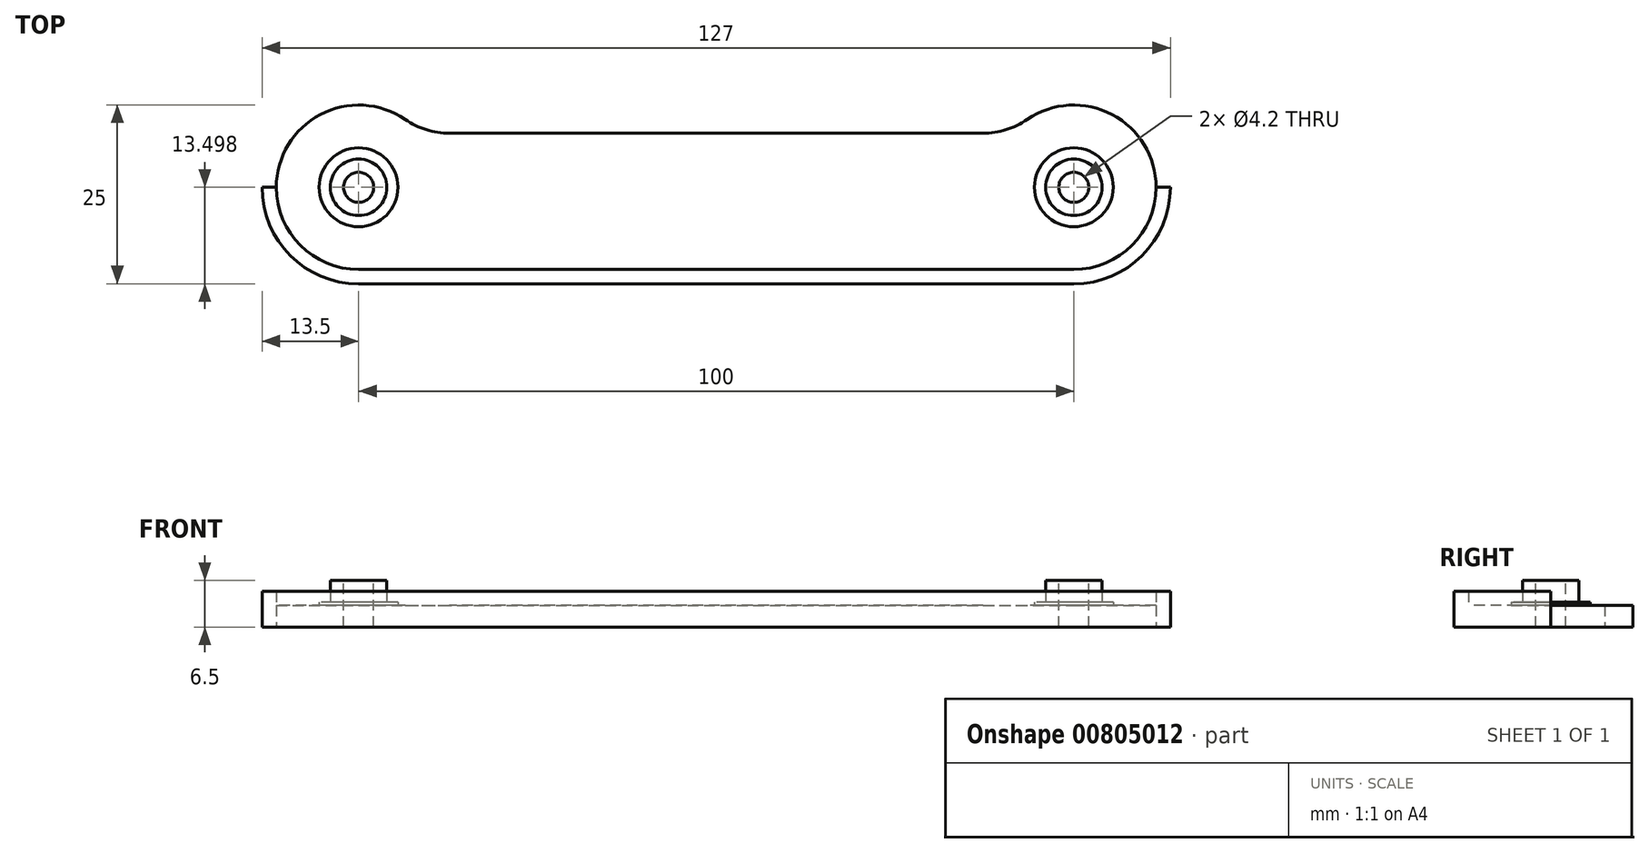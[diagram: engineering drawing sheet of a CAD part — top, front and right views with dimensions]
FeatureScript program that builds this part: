
annotation { "Feature Type Name" : "Feature", "Feature Type Description" : "" }
export const myFeature = defineFeature(function(context is Context, id is Id, definition is map)
    precondition{}
    {
        {
            var Q0;
            Q0=qCreatedBy(makeId("Top.planeOp"),FACE);
            var sketch = newSketch(context, id + "F0", { "sketchPlane" : qUnion([Q0])});
            skLineSegment(sketch, "E0", {"start": v(-50, -12.51) * mm, "end": v(0, -12.51) * mm});
            skArc(sketch, "E1", {"start": v(-50, -12.51) * mm, "mid": v(-61.5, -1.01) * mm, "end": v(-50, 10.49) * mm});
            skArc(sketch, "E2", {"start": v(-50, 10.49) * mm, "mid": v(-46.6, 9.97) * mm, "end": v(-43.5, 8.47) * mm});
            skArc(sketch, "E3", {"start": v(-43.5, 8.47) * mm, "mid": v(-40.54, 7.04) * mm, "end": v(-37.3, 6.55) * mm});
            skLineSegment(sketch, "E4", {"start": v(-37.3, 6.55) * mm, "end": v(0, 6.55) * mm});
            skLineSegment(sketch, "E5.MirrorCS", {"start": v(37.3, 6.55) * mm, "end": v(0, 6.55) * mm});
            skLineSegment(sketch, "E6.MirrorCS", {"start": v(50, -12.51) * mm, "end": v(0, -12.51) * mm});
            skArc(sketch, "E7.MirrorCS", {"start": v(50, -12.51) * mm, "mid": v(61.5, -1.01) * mm, "end": v(50, 10.49) * mm});
            skArc(sketch, "E8.MirrorCS", {"start": v(50, 10.49) * mm, "mid": v(46.6, 9.97) * mm, "end": v(43.5, 8.47) * mm});
            skArc(sketch, "E9.MirrorCS", {"start": v(43.5, 8.47) * mm, "mid": v(40.54, 7.04) * mm, "end": v(37.3, 6.55) * mm});
            skSolve(sketch);
        }
        {
            var Q0;
            Q0 = qSketchRegion(id + "F0", true);
            extrude(context, id + "F1", {"entities" : qUnion([Q0]), "depth" : 3 * mm, "offsetDistance" : 25 * mm});
        }
        {
            var Q0;
            Q0=makeQuery(id+"F0.imprint","IMPRINT",FACE,{"disambiguationData":[TD([[makeQuery(id+"F0.imprint","IMPRINT",EDGE,{"derivedFrom":sQuery(id+"F0.wireOp",EDGE,"E0")}),1.0]])]});
            var sketch = newSketch(context, id + "F2", { "sketchPlane" : qUnion([Q0])});
            skLineSegment(sketch, "E10.0", {"start": v(-50, -14.51) * mm, "end": v(50, -14.51) * mm});
            skArc(sketch, "E10.3", {"start": v(50, -14.51) * mm, "mid": v(59.55, -10.56) * mm, "end": v(63.5, -1.01) * mm});
            skArc(sketch, "E10.5", {"start": v(-63.5, -1.01) * mm, "mid": v(-59.55, -10.56) * mm, "end": v(-50, -14.51) * mm});
            skArc(sketch, "E11.0.0", {"start": v(50, -12.51) * mm, "mid": v(58.13, -9.14) * mm, "end": v(61.5, -1.01) * mm});
            skArc(sketch, "E11.0.4", {"start": v(-61.5, -1.01) * mm, "mid": v(-58.13, -9.14) * mm, "end": v(-50, -12.51) * mm});
            skLineSegment(sketch, "E11.0.5", {"start": v(-50, -12.51) * mm, "end": v(50, -12.51) * mm});
            skLineSegment(sketch, "E12", {"start": v(-61.5, -1.01) * mm, "end": v(-63.5, -1.01) * mm});
            skLineSegment(sketch, "E13.MirrorCS", {"start": v(61.5, -1.01) * mm, "end": v(63.5, -1.01) * mm});
            skPoint(sketch, "E11.0.3.end.orphan", {"position": v(-43.5, 8.47) * mm});
            skPoint(sketch, "E11.0.2.end.orphan", {"position": v(-37.3, 6.55) * mm});
            skPoint(sketch, "E11.0.1.end.orphan", {"position": v(37.3, 6.55) * mm});
            skPoint(sketch, "E14.orphan", {"position": v(43.5, 8.47) * mm});
            skSolve(sketch);
        }
        {
            var Q0;
            Q0 = qSketchRegion(id + "F2", true);
            extrude(context, id + "F3", {"entities" : qUnion([Q0]), "operationType" : NewBodyOperationType.ADD, "depth" : 5 * mm, "offsetDistance" : 25 * mm});
        }
        {
            var Q0;
            Q0=makeQuery(id+"F1.opExtrude","CAP_FACE",FACE,{"disambiguationData":[OSD([sQuery(id+"F0.wireOp",EDGE,"E0"),sQuery(id+"F0.wireOp",EDGE,"E1"),sQuery(id+"F0.wireOp",EDGE,"E2"),sQuery(id+"F0.wireOp",EDGE,"E3"),sQuery(id+"F0.wireOp",EDGE,"E4"),sQuery(id+"F0.wireOp",EDGE,"E5.MirrorCS"),sQuery(id+"F0.wireOp",EDGE,"E6.MirrorCS"),sQuery(id+"F0.wireOp",EDGE,"E7.MirrorCS"),sQuery(id+"F0.wireOp",EDGE,"E8.MirrorCS"),sQuery(id+"F0.wireOp",EDGE,"E9.MirrorCS")])],"isStart":false});
            var sketch = newSketch(context, id + "F4", { "sketchPlane" : qUnion([Q0])});
            skCircle(sketch, "E15", {"center": v(-50, -1.01) * mm, "radius": 3.95 * mm});
            skCircle(sketch, "E16.MirrorC", {"center": v(50, -1.01) * mm, "radius": 3.95 * mm});
            skSolve(sketch);
        }
        {
            var Q0;
            Q0 = qSketchRegion(id + "F4", true);
            extrude(context, id + "F5", {"entities" : qUnion([Q0]), "operationType" : NewBodyOperationType.ADD, "depth" : 3.5 * mm, "offsetDistance" : 25 * mm});
        }
        {
            var Q0;
            Q0=makeQuery(id+"F5.opExtrude","CAP_FACE",FACE,{"disambiguationData":[OSD([sQuery(id+"F4.wireOp",EDGE,"E15")])],"isStart":false});
            var sketch = newSketch(context, id + "F6", { "sketchPlane" : qUnion([Q0])});
            skCircle(sketch, "E17", {"center": v(-50, -1.01) * mm, "radius": 2.1 * mm});
            skCircle(sketch, "E18.MirrorC", {"center": v(50, -1.01) * mm, "radius": 2.1 * mm});
            skSolve(sketch);
        }
        {
            var Q0;
            Q0 = qSketchRegion(id + "F6", true);
            extrude(context, id + "F7", {"entities" : qUnion([Q0]), "operationType" : NewBodyOperationType.REMOVE, "oppositeDirection" : true, "depth" : 25 * mm, "offsetDistance" : 25 * mm});
        }
        {
            var Q0;
            Q0=makeQuery(id+"F1.opExtrude","CAP_FACE",FACE,{"disambiguationData":[OSD([sQuery(id+"F0.wireOp",EDGE,"E0"),sQuery(id+"F0.wireOp",EDGE,"E1"),sQuery(id+"F0.wireOp",EDGE,"E2"),sQuery(id+"F0.wireOp",EDGE,"E3"),sQuery(id+"F0.wireOp",EDGE,"E4"),sQuery(id+"F0.wireOp",EDGE,"E5.MirrorCS"),sQuery(id+"F0.wireOp",EDGE,"E6.MirrorCS"),sQuery(id+"F0.wireOp",EDGE,"E7.MirrorCS"),sQuery(id+"F0.wireOp",EDGE,"E8.MirrorCS"),sQuery(id+"F0.wireOp",EDGE,"E9.MirrorCS")])],"isStart":false});
            var sketch = newSketch(context, id + "F8", { "sketchPlane" : qUnion([Q0])});
            skCircle(sketch, "E19", {"center": v(-50, -1.01) * mm, "radius": 5.51 * mm});
            skCircle(sketch, "E20.0", {"center": v(-50, -1.01) * mm, "radius": 3.95 * mm});
            skCircle(sketch, "E21.MirrorC", {"center": v(50, -1.01) * mm, "radius": 3.95 * mm});
            skCircle(sketch, "E22.MirrorC", {"center": v(50, -1.01) * mm, "radius": 5.51 * mm});
            skSolve(sketch);
        }
        {
            var Q0;
            Q0 = qSketchRegion(id + "F8", true);
            extrude(context, id + "F9", {"entities" : qUnion([Q0]), "operationType" : NewBodyOperationType.ADD, "depth" : 0.5 * mm, "offsetDistance" : 25 * mm});
        }
    });
